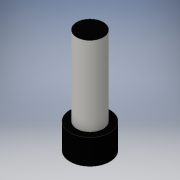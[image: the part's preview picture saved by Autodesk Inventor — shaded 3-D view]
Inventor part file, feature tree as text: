
AUTODESK INVENTOR PART (.ipt)
format: ipt  version: 2016 (Build 200138000, 138)  size: 101,376 bytes
history: native  units: in
note: dims shown in document units (in); Inventor stores cm internally (conversion verified against a paired STEP export)
features: extrude x2, sketch x2
ambient origin geometry x8: Origin, YZ Plane, XZ Plane, XY Plane, X Axis, Y Axis, Z Axis, Center Point
bodies: Solid1 (feature_tree)
feature tree (4):
  extrude  "Extrusion1"  Depth=0.1496in TaperAngle=0.0deg
  extrude  "Extrusion2"  Depth=0.4724in TaperAngle=0.0deg
  sketch  "Sketch1"  dims[d0=0.2362in d1=0.1496in d2=0.0in]
  sketch  "Sketch2"  dims[d3=0.1575in d4=0.4724in d5=0.0in]
